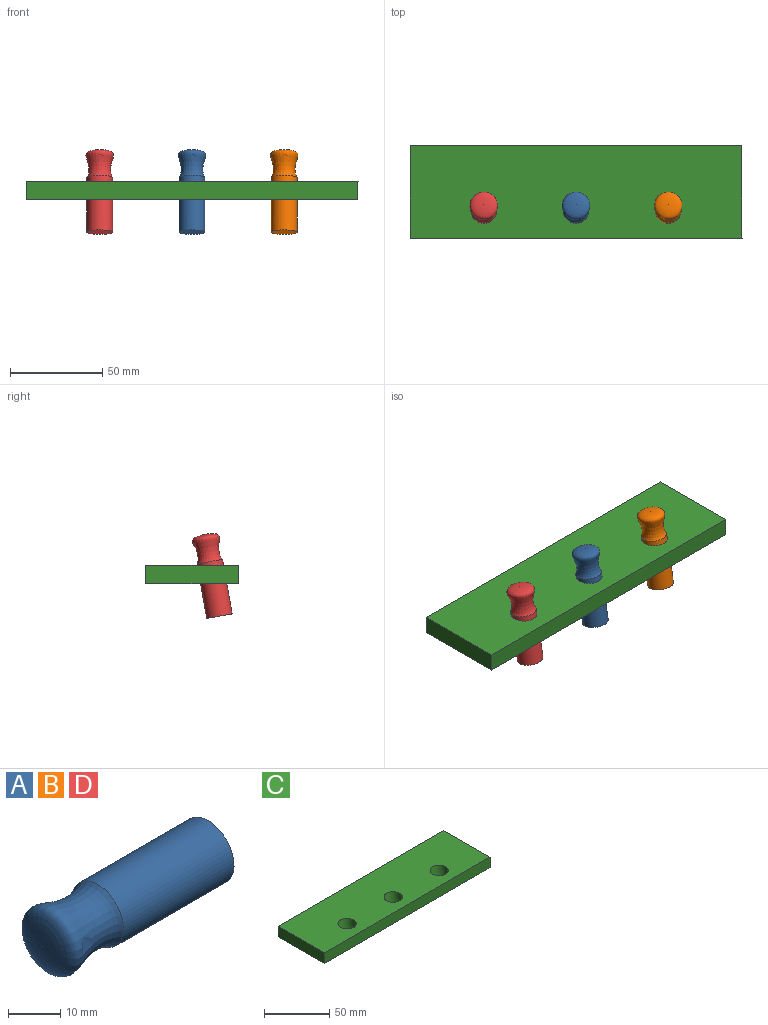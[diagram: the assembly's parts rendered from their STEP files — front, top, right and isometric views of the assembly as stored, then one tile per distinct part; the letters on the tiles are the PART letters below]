
ASSEMBLY  parts=4 mates=1
PART A: 3 faces, bbox 45x15x15 mm
  f0: revolved ~15.02x15.02mm, area 742.3mm2, adj f2
  f1: plane 14x14mm, normal (1,0,0), area 153.9mm2, adj f2
  f2: cylinder r=7mm len=30mm, axis (-1,0,0), area 1319.5mm2, adj f0,f1
PART B: same geometry as A
PART C: 9 faces, bbox 180x50x14.9 mm
  f0: plane 180x10mm, normal (0,1,0), area 1800mm2, adj f1,f3,f4,f5
  f1: plane 50x10mm, normal (-1,0,0), area 500mm2, adj f0,f2,f4,f5
  f2: plane 180x10mm, normal (0,-1,0), area 1800mm2, adj f1,f3,f4,f5
  f3: plane 50x10mm, normal (1,0,0), area 500mm2, adj f0,f2,f4,f5
  f4: plane 180x50mm, normal (0,0,1), area 8531.1mm2, adj f0,f1,f2,f3,f6,f7,f8
  f5: plane 180x50mm, normal (0,0,-1), area 8531.1mm2, adj f0,f1,f2,f3,f6,f7,f8
  f6: cylinder r=7mm len=15.98mm, axis (0,0.17,0.98), area 446.6mm2, adj f4,f5
  f7: cylinder r=7mm len=15.98mm, axis (0,0.17,0.98), area 446.6mm2, adj f4,f5
  f8: cylinder r=7mm len=15.98mm, axis (0,0.17,0.98), area 446.6mm2, adj f4,f5
PART D: same geometry as A
PLACE A rot(axis=(-0.09,0.99,-0.09),90.4deg) t=(6.12,-26.29,29.35)mm
PLACE B rot(axis=(-0.09,0.99,-0.09),90.4deg) t=(56.12,-26.29,29.35)mm
PLACE C rot(axis=(-0.08,0.56,0.82),0deg) t=(6.12,-19.23,2.69)mm
PLACE D rot(axis=(-0.09,0.99,-0.09),90.4deg) t=(-43.88,-26.29,29.35)mm
MATE slider D.f2 <-> C.f7  axis (0,0.17,0.98) through (-43.88,-31.5,-0.19)mm
